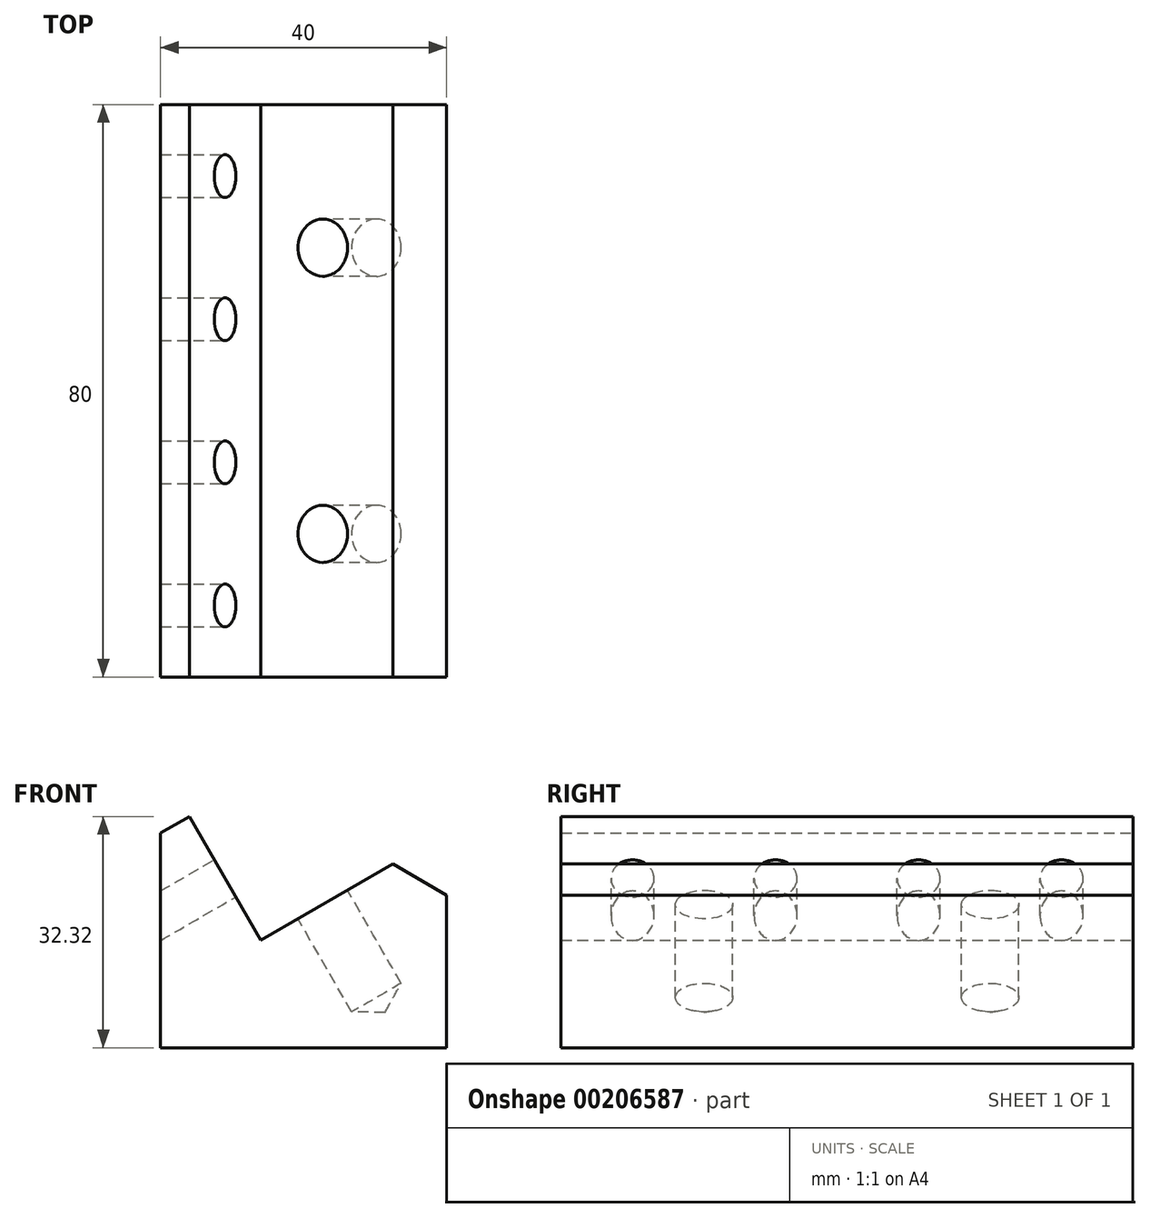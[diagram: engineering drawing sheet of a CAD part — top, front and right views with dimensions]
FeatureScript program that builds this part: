
annotation { "Feature Type Name" : "Feature", "Feature Type Description" : "" }
export const myFeature = defineFeature(function(context is Context, id is Id, definition is map)
    precondition{}
    {
        {
            var Q0;
            Q0=qCreatedBy(makeId("Front.planeOp"),FACE);
            var sketch = newSketch(context, id + "F0", { "sketchPlane" : qUnion([Q0])});
            skLineSegment(sketch, "E0", {"start": v(-41.74, 13.08) * mm, "end": v(-41.74, -16.92) * mm});
            skLineSegment(sketch, "E1", {"start": v(-41.74, -16.92) * mm, "end": v(-1.74, -16.92) * mm});
            skLineSegment(sketch, "E2", {"start": v(-1.74, -16.92) * mm, "end": v(-1.74, 13.08) * mm});
            skLineSegment(sketch, "E3", {"start": v(-1.74, 13.08) * mm, "end": v(-27.72, -1.92) * mm});
            skLineSegment(sketch, "E4", {"start": v(-27.72, -1.92) * mm, "end": v(-37.72, 15.4) * mm});
            skLineSegment(sketch, "E5", {"start": v(-37.72, 15.4) * mm, "end": v(-41.74, 13.08) * mm});
            skSolve(sketch);
        }
        {
            var Q0;
            Q0=makeQuery(id+"F0.imprint","IMPRINT",FACE,{"disambiguationData":[TD([[makeQuery(id+"F0.imprint","IMPRINT",EDGE,{"derivedFrom":sQuery(id+"F0.wireOp",EDGE,"E0")}),1.0]])]});
            extrude(context, id + "F1", {"entities" : qUnion([Q0]), "depth" : 80 * mm});
        }
        {
            var Q0;
            Q0=makeQuery(id+"F1.opExtrude","SWEPT_FACE",FACE,{"disambiguationData":[OSD([sQuery(id+"F0.wireOp",EDGE,"E3")])]});
            var sketch = newSketch(context, id + "F2", { "sketchPlane" : qUnion([Q0])});
            skPoint(sketch, "E6", {"position": v(-14.97, -20) * mm});
            skPoint(sketch, "E7", {"position": v(-14.97, -60) * mm});
            skSolve(sketch);
        }
        {
            var Q0;
            Q0=sQuery(id+"F2.wireOp",VERTEX,"E7");
            var Q1;
            Q1=sQuery(id+"F2.wireOp",VERTEX,"E6");
            var Q2;
            Q2=makeQuery(id+"F1.opExtrude","SWEPT_BODY",BODY,{"disambiguationData":[OSD([sQuery(id+"F0.wireOp",EDGE,"E0"),sQuery(id+"F0.wireOp",EDGE,"E1"),sQuery(id+"F0.wireOp",EDGE,"E2"),sQuery(id+"F0.wireOp",EDGE,"E3"),sQuery(id+"F0.wireOp",EDGE,"E4"),sQuery(id+"F0.wireOp",EDGE,"E5")])]});
            hole(context, id + "F3", {"style" : HoleStyle.SIMPLE, "endStyle" : HoleEndStyle.BLIND, "holeDiameter" : 8 * mm, "holeDepth" : 15 * mm, "locations" : qUnion([Q0, Q1]), "scope" : qUnion([Q2])});
        }
        {
            var Q0;
            Q0=makeQuery(id+"F1.opExtrude","SWEPT_EDGE",EDGE,{"disambiguationData":[OSD([sQuery(id+"F0.wireOp",EDGE,"E2"),sQuery(id+"F0.wireOp",EDGE,"E3")])]});
            chamfer(context, id + "F4", {"entities" : qUnion([Q0]), "width" : 5 * mm, "tangentPropagation" : true});
        }
        {
            var Q0;
            Q0=makeQuery(id+"F1.opExtrude","SWEPT_FACE",FACE,{"disambiguationData":[OSD([sQuery(id+"F0.wireOp",EDGE,"E4")])]});
            var sketch = newSketch(context, id + "F5", { "sketchPlane" : qUnion([Q0])});
            skPoint(sketch, "E8", {"position": v(-70, 22.2) * mm});
            skPoint(sketch, "E9", {"position": v(-50, 22.2) * mm});
            skPoint(sketch, "E10", {"position": v(-30, 22.2) * mm});
            skPoint(sketch, "E11", {"position": v(-10, 22.2) * mm});
            skSolve(sketch);
        }
        {
            var Q0;
            Q0=sQuery(id+"F5.wireOp",VERTEX,"E8");
            var Q1;
            Q1=sQuery(id+"F5.wireOp",VERTEX,"E9");
            var Q2;
            Q2=sQuery(id+"F5.wireOp",VERTEX,"E10");
            var Q3;
            Q3=sQuery(id+"F5.wireOp",VERTEX,"E11");
            var Q4;
            Q4=makeQuery(id+"F1.opExtrude","SWEPT_BODY",BODY,{"disambiguationData":[OSD([sQuery(id+"F0.wireOp",EDGE,"E0"),sQuery(id+"F0.wireOp",EDGE,"E1"),sQuery(id+"F0.wireOp",EDGE,"E2"),sQuery(id+"F0.wireOp",EDGE,"E3"),sQuery(id+"F0.wireOp",EDGE,"E4"),sQuery(id+"F0.wireOp",EDGE,"E5")])]});
            hole(context, id + "F6", {"style" : HoleStyle.SIMPLE, "endStyle" : HoleEndStyle.THROUGH, "holeDiameter" : 6 * mm, "locations" : qUnion([Q0, Q1, Q2, Q3]), "scope" : qUnion([Q4]), "isTappedThrough" : true});
        }
    });
